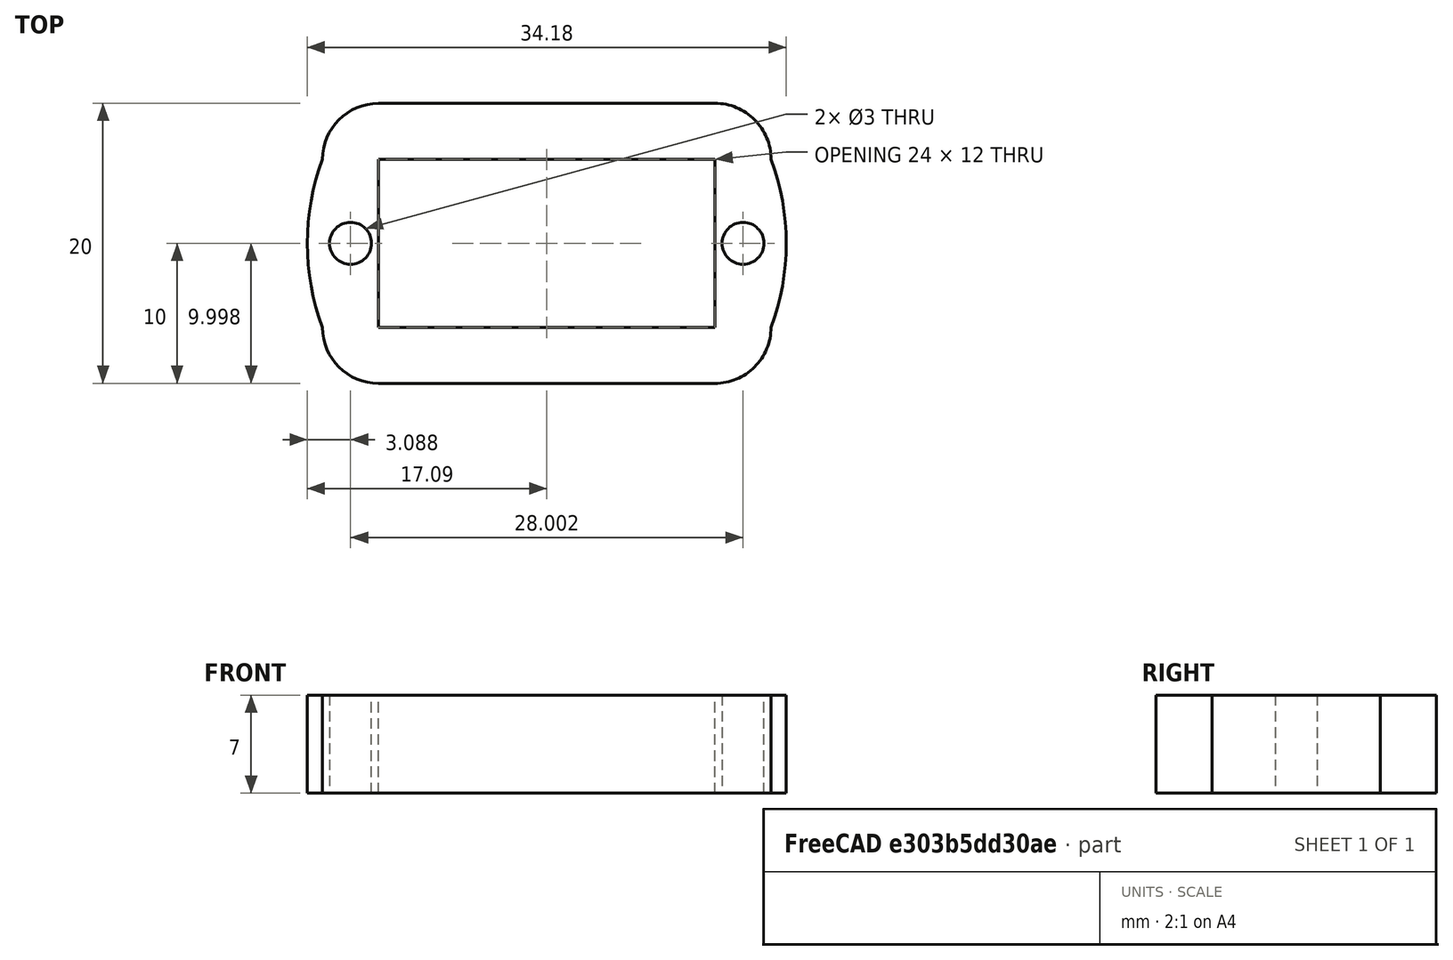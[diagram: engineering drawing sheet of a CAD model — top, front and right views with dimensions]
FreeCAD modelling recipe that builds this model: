
FCSTD DOCUMENT  (FreeCAD 1.0R39109 (Git))
Label: servo_sleeve
License: All rights reserved
LicenseURL: https://en.wikipedia.org/wiki/All_rights_reserved
objects: Sketcher::SketchObject×1, PartDesign::Pad×1, PartDesign::Body×1
note: 6 computed .brp shape members not serialized (recipe doc carries the construction recipe); baked Part::Feature solids carry a one-line shape summary decoded from their .brp

FEATURE [Sketcher::SketchObject] Sketch
  ArcFitTolerance = 1e-06
  AttachmentSupport = -> [XY_Plane]
  FullyConstrained = false
  MakeInternals = false
  MapMode = 5
  sketch-geometry (20):
    g0: LineSegment StartX=0 StartY=0 StartZ=0 EndX=24.0006 EndY=0 EndZ=0
    g1: LineSegment StartX=0 StartY=0 StartZ=0 EndX=0 EndY=4.5 EndZ=0
    g2: LineSegment StartX=0 StartY=7.5 StartZ=0 EndX=0 EndY=12 EndZ=0
    g3: LineSegment StartX=0 StartY=12 StartZ=0 EndX=24.0006 EndY=12 EndZ=0
    g4: LineSegment StartX=24.0006 StartY=12 StartZ=0 EndX=24.0006 EndY=7.5 EndZ=0
    g5: LineSegment StartX=24.0006 StartY=4.5 StartZ=0 EndX=24.0006 EndY=0 EndZ=0
    g6: GeomPoint X=27.9998 Y=5.99891 Z=0
    g7: LineSegment StartX=0 StartY=15.9975 StartZ=0 EndX=24 EndY=15.9975 EndZ=0
    g8: LineSegment StartX=-7e-16 StartY=-3.99818 StartZ=0 EndX=24 EndY=-3.99818 EndZ=0
    g9: LineSegment StartX=24.0006 StartY=7.5 StartZ=0 EndX=24.0006 EndY=4.5 EndZ=0
    g10: ArcOfCircle CenterX=0 CenterY=12 CenterZ=0 NormalX=0 NormalY=0 NormalZ=1 AngleXU=0 Radius=3.99755 StartAngle=1.5708 EndAngle=3.14159
    g11: ArcOfCircle CenterX=0 CenterY=0 CenterZ=0 NormalX=0 NormalY=0 NormalZ=1 AngleXU=0 Radius=3.99818 StartAngle=3.14159 EndAngle=4.71239
    g12: ArcOfCircle CenterX=24.0006 CenterY=0 CenterZ=0 NormalX=0 NormalY=0 NormalZ=1 AngleXU=0 Radius=3.99818 StartAngle=4.71223 EndAngle=6.28319
    g13: ArcOfCircle CenterX=24.0006 CenterY=12 CenterZ=0 NormalX=0 NormalY=0 NormalZ=1 AngleXU=0 Radius=3.99755 StartAngle=6.28319 EndAngle=7.85414
    g14: LineSegment StartX=0 StartY=7.5 StartZ=0 EndX=0 EndY=4.5 EndZ=0
    g15: Circle CenterX=-2.0015 CenterY=5.9988 CenterZ=0 NormalX=0 NormalY=0 NormalZ=1 AngleXU=0 Radius=1.5
    g16: Circle CenterX=26.0007 CenterY=5.99851 CenterZ=0 NormalX=0 NormalY=0 NormalZ=1 AngleXU=0 Radius=1.5
    g17: GeomPoint X=11.9998 Y=5.99915 Z=0
    g18: ArcOfCircle CenterX=11.9998 CenterY=5.99915 CenterZ=0 NormalX=0 NormalY=0 NormalZ=1 AngleXU=0 Radius=17.0858 StartAngle=2.78272 EndAngle=3.50036
    g19: ArcOfCircle CenterX=11.9998 CenterY=5.99915 CenterZ=0 NormalX=0 NormalY=0 NormalZ=1 AngleXU=0 Radius=17.0868 StartAngle=5.92444 EndAngle=6.64204
  constraints (40):
    c: Coincident(g0,g-1)
    c: PointOnObject(g0,g-1)
    c: Coincident(g1,g0)
    c: PointOnObject(g1,g-2)
    c: PointOnObject(g2,g-2)
    c: PointOnObject(g2,g-2)
    c: Coincident(g3,g2)
    c: Horizontal(g3)
    c: Coincident(g4,g3)
    c: Vertical(g4)
    c: Coincident(g5,g0)
    c: Distance(g7) = 24
    c: Horizontal(g7)
    c: PointOnObject(g7,g-2)
    c: Distance(g8) = 24
    c: Horizontal(g8)
    c: PointOnObject(g8,g-2)
    c: PointOnObject(g11,g-1)
    c: PointOnObject(g12,g-1)
    c: Coincident(g9,g4)
    c: Coincident(g9,g5)
    c: Vertical(g9)
    c: Coincident(g10,g2)
    c: Coincident(g10,g7)
    c: Coincident(g11,g0)
    c: Coincident(g11,g8)
    c: Coincident(g12,g0)
    c: Coincident(g12,g8)
    c: Coincident(g13,g3)
    c: Coincident(g13,g7)
    c: Coincident(g14,g2)
    c: Coincident(g14,g1)
    c: Diameter(g15) = 3
    c: Diameter(g16) = 3
    c: Coincident(g18,g17)
    c: Coincident(g18,g10)
    c: Coincident(g18,g11)
    c: Coincident(g19,g17)
    c: Coincident(g19,g13)
    c: Coincident(g19,g12)
FEATURE [PartDesign::Pad] Pad
  Direction = (0,0,1)
  Length = 7
  Length2 = 10
  Profile = -> Sketch
  ReferenceAxis = -> Sketch [N_Axis]
  Refine = true
  Suppressed = false
  Type = 0
FEATURE [PartDesign::Body] Body
  AllowCompound = false
  Group = -> [Sketch,Pad]
  Origin = -> Origin
  Tip = -> Pad
